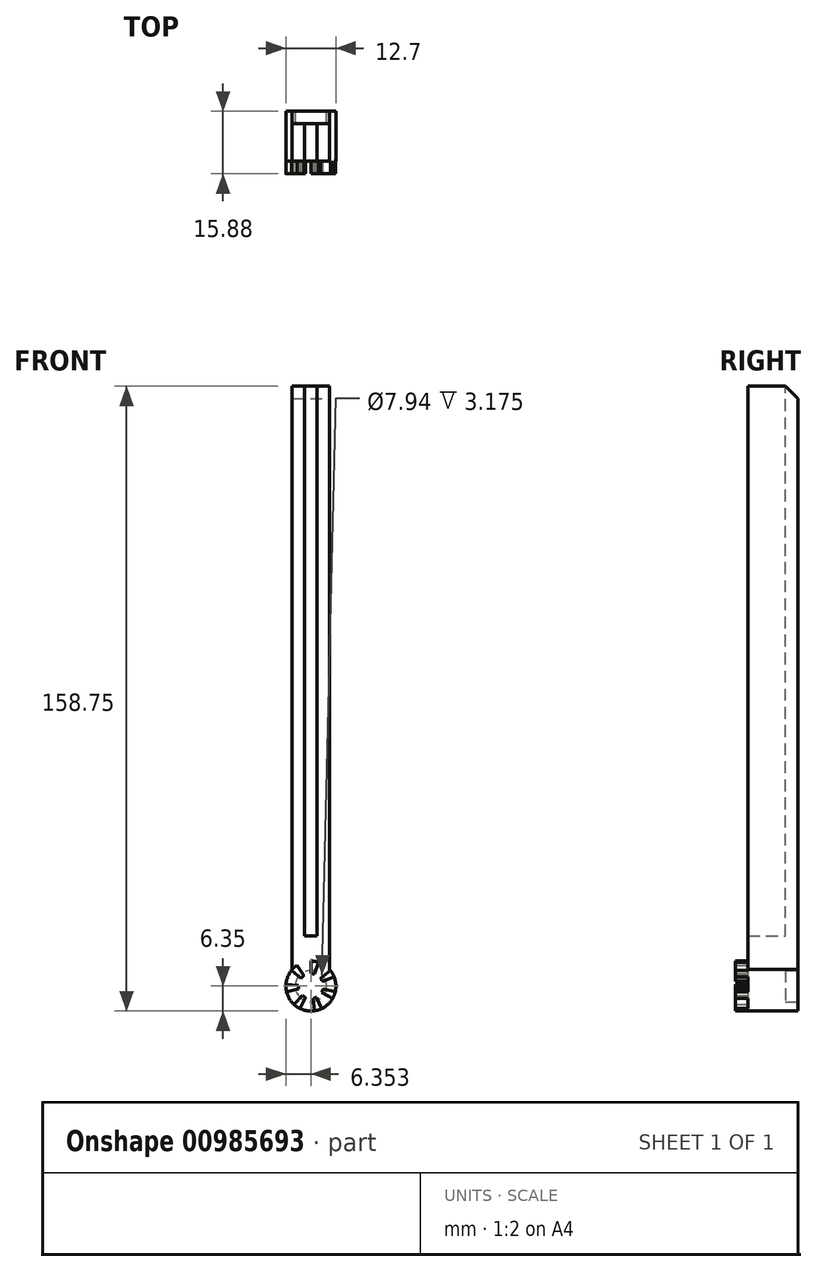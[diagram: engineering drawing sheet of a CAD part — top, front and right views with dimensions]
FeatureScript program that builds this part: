
annotation { "Feature Type Name" : "Feature", "Feature Type Description" : "" }
export const myFeature = defineFeature(function(context is Context, id is Id, definition is map)
    precondition{}
    {
        {
            var Q0;
            Q0=qCreatedBy(makeId("Front.planeOp"),FACE);
            var sketch = newSketch(context, id + "F0", { "sketchPlane" : qUnion([Q0])});
            skLineSegment(sketch, "E0.bottom", {"start": v(0, 0) * mm, "end": v(9.53, 0) * mm});
            skLineSegment(sketch, "E0.top", {"start": v(0, 152.4) * mm, "end": v(9.52, 152.4) * mm});
            skLineSegment(sketch, "E0.left", {"start": v(0, 0) * mm, "end": v(0, 152.4) * mm});
            skLineSegment(sketch, "E0.right", {"start": v(9.53, 0) * mm, "end": v(9.52, 152.4) * mm});
            skCircle(sketch, "E1", {"center": v(4.76, 0) * mm, "radius": 6.35 * mm});
            skSolve(sketch);
        }
        {
            var Q0;
            {var subQ0=sQuery(id+"F0.wireOp",EDGE,"E0.top");Q0=makeQuery(id+"F0.imprint","IMPRINT",FACE,{"disambiguationData":[TD([[makeQuery(id+"F0.imprint","IMPRINT",EDGE,{"derivedFrom":subQ0}),-1.0]])]});}
            var Q1;
            {var subQ0=sQuery(id+"F0.wireOp",EDGE,"E0.bottom");Q1=makeQuery(id+"F0.imprint","IMPRINT",FACE,{"disambiguationData":[TD([[makeQuery(id+"F0.imprint","IMPRINT",EDGE,{"derivedFrom":subQ0}),1.0]])]});}
            var Q2;
            {var subQ0=sQuery(id+"F0.wireOp",EDGE,"E0.bottom");Q2=makeQuery(id+"F0.imprint","IMPRINT",FACE,{"disambiguationData":[TD([[makeQuery(id+"F0.imprint","IMPRINT",EDGE,{"derivedFrom":subQ0}),-1.0]])]});}
            extrude(context, id + "F1", {"entities" : qUnion([Q0, Q1, Q2]), "depth" : 12.7 * mm, "offsetDistance" : 25.4 * mm});
        }
        {
            var Q0;
            Q0=makeQuery(id+"F1.opExtrude","SWEPT_FACE",FACE,{"disambiguationData":[OSD([sQuery(id+"F0.wireOp",EDGE,"E0.top")])]});
            var sketch = newSketch(context, id + "F2", { "sketchPlane" : qUnion([Q0])});
            skLineSegment(sketch, "E2.bottom", {"start": v(3.18, -12.7) * mm, "end": v(6.35, -12.7) * mm});
            skLineSegment(sketch, "E2.top", {"start": v(3.17, -3.18) * mm, "end": v(6.35, -3.18) * mm});
            skLineSegment(sketch, "E2.left", {"start": v(3.18, -12.7) * mm, "end": v(3.17, -3.18) * mm});
            skLineSegment(sketch, "E2.right", {"start": v(6.35, -12.7) * mm, "end": v(6.35, -3.18) * mm});
            skSolve(sketch);
        }
        {
            var Q0;
            Q0=makeQuery(id+"F2.imprint","IMPRINT",FACE,{"disambiguationData":[TD([[makeQuery(id+"F2.imprint","IMPRINT",EDGE,{"derivedFrom":sQuery(id+"F2.wireOp",EDGE,"E2.bottom")}),1.0]])]});
            extrude(context, id + "F3", {"entities" : qUnion([Q0]), "operationType" : NewBodyOperationType.REMOVE, "oppositeDirection" : true, "depth" : 139.7 * mm, "offsetDistance" : 25.4 * mm});
        }
        {
            var Q0;
            Q0=makeQuery(id+"F1.opExtrude","CAP_FACE",FACE,{"disambiguationData":[OSD([sQuery(id+"F0.wireOp",EDGE,"E0.top"),sQuery(id+"F0.wireOp",EDGE,"E0.left"),sQuery(id+"F0.wireOp",EDGE,"E0.right"),sQuery(id+"F0.wireOp",EDGE,"E1")])],"isStart":false});
            var sketch = newSketch(context, id + "F4", { "sketchPlane" : qUnion([Q0])});
            skArc(sketch, "E3", {"start": v(2.97, 2.62) * mm, "mid": v(2.6, 2.33) * mm, "end": v(2.28, 1.98) * mm});
            skArc(sketch, "E4", {"start": v(1.19, 5.25) * mm, "mid": v(0.44, 4.65) * mm, "end": v(-0.2, 3.96) * mm});
            skLineSegment(sketch, "E5", {"start": v(4.76, 3.18) * mm, "end": v(4.76, 6.35) * mm});
            skPoint(sketch, "E6.center", {"position": v(0, 0) * mm});
            skLineSegment(sketch, "E7.2.0", {"start": v(2.97, 2.62) * mm, "end": v(1.19, 5.25) * mm});
            skLineSegment(sketch, "E7.3.0", {"start": v(2.28, 1.98) * mm, "end": v(-0.2, 3.96) * mm});
            skLineSegment(sketch, "E7.5.0", {"start": v(1.6, 0.24) * mm, "end": v(-1.57, 0.47) * mm});
            skLineSegment(sketch, "E7.6.0", {"start": v(1.67, -0.7) * mm, "end": v(-1.43, -1.41) * mm});
            skLineSegment(sketch, "E7.8.0", {"start": v(2.6, -2.33) * mm, "end": v(0.44, -4.65) * mm});
            skLineSegment(sketch, "E7.9.0", {"start": v(3.38, -2.86) * mm, "end": v(2, -5.72) * mm});
            skLineSegment(sketch, "E7.11.0", {"start": v(5.24, -3.14) * mm, "end": v(5.7, -6.28) * mm});
            skLineSegment(sketch, "E7.12.0", {"start": v(6.14, -2.86) * mm, "end": v(7.52, -5.72) * mm});
            skLineSegment(sketch, "E7.14.0", {"start": v(7.51, -1.59) * mm, "end": v(10.26, -3.18) * mm});
            skLineSegment(sketch, "E7.15.0", {"start": v(7.86, -0.7) * mm, "end": v(10.95, -1.41) * mm});
            skLineSegment(sketch, "E7.17.0", {"start": v(7.72, 1.16) * mm, "end": v(10.67, 2.32) * mm});
            skLineSegment(sketch, "E7.18.0", {"start": v(7.24, 1.98) * mm, "end": v(9.73, 3.96) * mm});
            skLineSegment(sketch, "E8.1.20.0", {"start": v(5.7, 3.03) * mm, "end": v(6.63, 6.07) * mm});
            skArc(sketch, "E9.trimOffspring", {"start": v(5.7, 3.03) * mm, "mid": v(5.24, 3.14) * mm, "end": v(4.76, 3.18) * mm});
            skArc(sketch, "E10.trimOffspring", {"start": v(7.72, 1.16) * mm, "mid": v(7.51, 1.59) * mm, "end": v(7.24, 1.98) * mm});
            skArc(sketch, "E11.trimOffspring", {"start": v(7.51, -1.59) * mm, "mid": v(7.72, -1.16) * mm, "end": v(7.86, -0.7) * mm});
            skArc(sketch, "E12.trimOffspring", {"start": v(5.24, -3.14) * mm, "mid": v(5.7, -3.03) * mm, "end": v(6.14, -2.86) * mm});
            skArc(sketch, "E13.trimOffspring", {"start": v(2.6, -2.33) * mm, "mid": v(2.97, -2.62) * mm, "end": v(3.38, -2.86) * mm});
            skArc(sketch, "E14.trimOffspring", {"start": v(1.6, 0.24) * mm, "mid": v(1.6, -0.24) * mm, "end": v(1.67, -0.7) * mm});
            skArc(sketch, "E15.trimOffspring", {"start": v(6.63, 6.07) * mm, "mid": v(5.7, 6.28) * mm, "end": v(4.76, 6.35) * mm});
            skArc(sketch, "E16.trimOffspring", {"start": v(10.67, 2.32) * mm, "mid": v(10.26, 3.17) * mm, "end": v(9.73, 3.96) * mm});
            skArc(sketch, "E17.trimOffspring", {"start": v(10.26, -3.18) * mm, "mid": v(10.67, -2.32) * mm, "end": v(10.95, -1.41) * mm});
            skArc(sketch, "E18.trimOffspring", {"start": v(5.7, -6.28) * mm, "mid": v(6.63, -6.07) * mm, "end": v(7.52, -5.72) * mm});
            skArc(sketch, "E19.trimOffspring", {"start": v(0.44, -4.65) * mm, "mid": v(1.19, -5.25) * mm, "end": v(2, -5.72) * mm});
            skArc(sketch, "E20.trimOffspring", {"start": v(-1.57, 0.47) * mm, "mid": v(-1.57, -0.47) * mm, "end": v(-1.43, -1.41) * mm});
            skSolve(sketch);
        }
        {
            var Q0;
            Q0=makeQuery(id+"F4.imprint","IMPRINT",FACE,{"disambiguationData":[TD([[makeQuery(id+"F4.imprint","IMPRINT",EDGE,{"derivedFrom":sQuery(id+"F4.wireOp",EDGE,"E7.11.0")}),1.0]])]});
            var Q1;
            Q1=makeQuery(id+"F4.imprint","IMPRINT",FACE,{"disambiguationData":[TD([[makeQuery(id+"F4.imprint","IMPRINT",EDGE,{"derivedFrom":sQuery(id+"F4.wireOp",EDGE,"E7.8.0")}),1.0]])]});
            var Q2;
            Q2=makeQuery(id+"F4.imprint","IMPRINT",FACE,{"disambiguationData":[TD([[makeQuery(id+"F4.imprint","IMPRINT",EDGE,{"derivedFrom":sQuery(id+"F4.wireOp",EDGE,"E7.5.0")}),1.0]])]});
            var Q3;
            Q3=makeQuery(id+"F4.imprint","IMPRINT",FACE,{"disambiguationData":[TD([[makeQuery(id+"F4.imprint","IMPRINT",EDGE,{"derivedFrom":sQuery(id+"F4.wireOp",EDGE,"E3")}),-1.0]])]});
            var Q4;
            Q4=makeQuery(id+"F4.imprint","IMPRINT",FACE,{"disambiguationData":[TD([[makeQuery(id+"F4.imprint","IMPRINT",EDGE,{"derivedFrom":sQuery(id+"F4.wireOp",EDGE,"E5")}),-1.0]])]});
            var Q5;
            Q5=makeQuery(id+"F4.imprint","IMPRINT",FACE,{"disambiguationData":[TD([[makeQuery(id+"F4.imprint","IMPRINT",EDGE,{"derivedFrom":sQuery(id+"F4.wireOp",EDGE,"E7.17.0")}),1.0]])]});
            var Q6;
            Q6=makeQuery(id+"F4.imprint","IMPRINT",FACE,{"disambiguationData":[TD([[makeQuery(id+"F4.imprint","IMPRINT",EDGE,{"derivedFrom":sQuery(id+"F4.wireOp",EDGE,"E7.14.0")}),1.0]])]});
            extrude(context, id + "F5", {"entities" : qUnion([Q0, Q1, Q2, Q3, Q4, Q5, Q6]), "operationType" : NewBodyOperationType.ADD, "depth" : 3.17 * mm, "offsetDistance" : 25.4 * mm});
        }
        {
            var Q0;
            Q0=makeQuery(id+"F1.opExtrude","CAP_FACE",FACE,{"disambiguationData":[OSD([sQuery(id+"F0.wireOp",EDGE,"E0.top"),sQuery(id+"F0.wireOp",EDGE,"E0.left"),sQuery(id+"F0.wireOp",EDGE,"E0.right"),sQuery(id+"F0.wireOp",EDGE,"E1")])],"isStart":true});
            var sketch = newSketch(context, id + "F6", { "sketchPlane" : qUnion([Q0])});
            skCircle(sketch, "E21", {"center": v(-4.76, 0) * mm, "radius": 3.97 * mm});
            skSolve(sketch);
        }
        {
            var Q0;
            Q0=makeQuery(id+"F6.imprint","IMPRINT",FACE,{"disambiguationData":[TD([[makeQuery(id+"F6.imprint","IMPRINT",EDGE,{"derivedFrom":sQuery(id+"F6.wireOp",EDGE,"E21")}),1.0]])]});
            extrude(context, id + "F7", {"entities" : qUnion([Q0]), "operationType" : NewBodyOperationType.REMOVE, "oppositeDirection" : true, "depth" : 3.17 * mm, "offsetDistance" : 25.4 * mm});
        }
        {
            var Q0;
            Q0=makeQuery(id+"F1.opExtrude","CAP_EDGE",EDGE,{"disambiguationData":[OSD([sQuery(id+"F0.wireOp",EDGE,"E0.top")])],"isStart":true});
            chamfer(context, id + "F8", {"entities" : qUnion([Q0]), "width" : 3.17 * mm, "tangentPropagation" : true});
        }
    });
